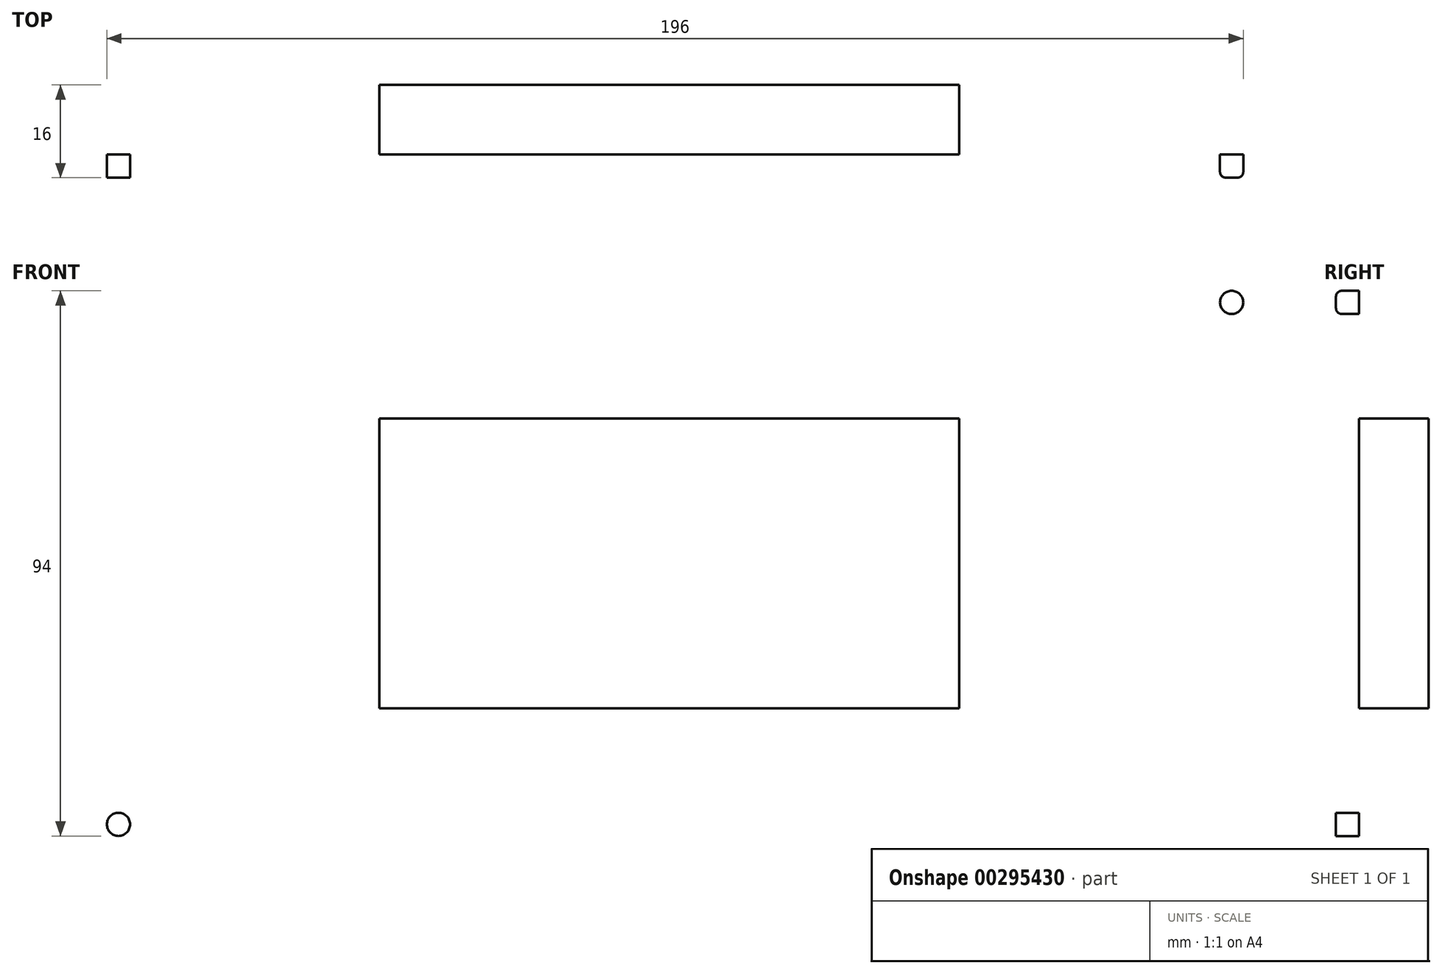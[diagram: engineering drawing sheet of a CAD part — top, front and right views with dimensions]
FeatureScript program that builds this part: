
annotation { "Feature Type Name" : "Feature", "Feature Type Description" : "" }
export const myFeature = defineFeature(function(context is Context, id is Id, definition is map)
    precondition{}
    {
        {
            var Q0;
            Q0=qCreatedBy(makeId("Front.planeOp"),FACE);
            var sketch = newSketch(context, id + "F0", { "sketchPlane" : qUnion([Q0])});
            skLineSegment(sketch, "E0.bottom", {"start": v(-188.88, 110.46) * mm, "end": v(13.12, 110.46) * mm});
            skLineSegment(sketch, "E0.top", {"start": v(-188.88, 10.46) * mm, "end": v(13.12, 10.46) * mm});
            skLineSegment(sketch, "E0.left", {"start": v(-188.88, 110.46) * mm, "end": v(-188.88, 10.46) * mm});
            skLineSegment(sketch, "E0.right", {"start": v(13.12, 110.46) * mm, "end": v(13.12, 10.46) * mm});
            skText(sketch, "E1", { "text": "// KARTA //", "fontName": "AllertaStencil-Regular.ttf"});
            const initialGuessF0  = {"E1": [-0.12488, 0.05579, 1, 0, 0.00936]};
            skSetInitialGuess(sketch, initialGuessF0);
            skSolve(sketch);
        }
        {
            var Q0;
            Q0=makeQuery(id+"F0.imprint","IMPRINT",FACE,{"disambiguationData":[TD([[makeQuery(id+"F0.imprint","IMPRINT",EDGE,{"derivedFrom":sQuery(id+"F0.wireOp",EDGE,"E0.bottom")}),-1.0]])]});
            extrude(context, id + "F1", {"entities" : qUnion([Q0]), "depth" : 4 * mm});
        }
        {
            var Q0;
            Q0=makeQuery(id+"F1.opExtrude","CAP_FACE",FACE,{"disambiguationData":[OSD([sQuery(id+"F0.wireOp",EDGE,"E0.bottom"),sQuery(id+"F0.wireOp",EDGE,"E0.top"),sQuery(id+"F0.wireOp",EDGE,"E0.left"),sQuery(id+"F0.wireOp",EDGE,"E0.right")])],"isStart":false});
            var sketch = newSketch(context, id + "F2", { "sketchPlane" : qUnion([Q0])});
            skLineSegment(sketch, "E2", {"start": v(-87.88, 10.46) * mm, "end": v(-87.88, 60.46) * mm, "construction": true});
            skPoint(sketch, "E2.endSnap0", {"position": v(-163.38, 60.46) * mm});
            skLineSegment(sketch, "E3", {"start": v(-163.38, 60.46) * mm, "end": v(-87.88, 60.46) * mm, "construction": true});
            skCircle(sketch, "E4", {"center": v(-183.88, 105.46) * mm, "radius": 2 * mm});
            skCircle(sketch, "E5.MirrorC", {"center": v(-183.88, 15.46) * mm, "radius": 2 * mm});
            skCircle(sketch, "E6.MirrorC", {"center": v(8.12, 105.46) * mm, "radius": 2 * mm});
            skCircle(sketch, "E7.MirrorC", {"center": v(8.12, 15.46) * mm, "radius": 2 * mm});
            skSolve(sketch);
        }
        {
            var Q0;
            Q0=makeQuery(id+"F2.imprint","IMPRINT",FACE,{"disambiguationData":[TD([[makeQuery(id+"F2.imprint","IMPRINT",EDGE,{"derivedFrom":sQuery(id+"F2.wireOp",EDGE,"E4")}),1.0]])]});
            var Q1;
            Q1=makeQuery(id+"F2.imprint","IMPRINT",FACE,{"disambiguationData":[TD([[makeQuery(id+"F2.imprint","IMPRINT",EDGE,{"derivedFrom":sQuery(id+"F2.wireOp",EDGE,"2b5eb0ab-fe42-49a6-bda5-95ec015d2c950.MirrorC")}),-1.0]])]});
            var Q2;
            Q2=makeQuery(id+"F2.imprint","IMPRINT",FACE,{"disambiguationData":[TD([[makeQuery(id+"F2.imprint","IMPRINT",EDGE,{"derivedFrom":sQuery(id+"F2.wireOp",EDGE,"2b5eb0ab-fe42-49a6-bda5-95ec015d2c951.MirrorC")}),1.0]])]});
            var Q3;
            Q3=makeQuery(id+"F2.imprint","IMPRINT",FACE,{"disambiguationData":[TD([[makeQuery(id+"F2.imprint","IMPRINT",EDGE,{"derivedFrom":sQuery(id+"F2.wireOp",EDGE,"E5.MirrorC")}),-1.0]])]});
            var Q4;
            Q4=makeQuery(id+"F2.imprint","IMPRINT",FACE,{"disambiguationData":[TD([[makeQuery(id+"F2.imprint","IMPRINT",EDGE,{"derivedFrom":sQuery(id+"F2.wireOp",EDGE,"V1kDyeQm-8hri-Xp3O-SjeW-TMvqUFOvwADP")}),1.0]])]});
            var Q5;
            Q5=makeQuery(id+"F2.imprint","IMPRINT",FACE,{"disambiguationData":[TD([[makeQuery(id+"F2.imprint","IMPRINT",EDGE,{"derivedFrom":sQuery(id+"F2.wireOp",EDGE,"Exs6iu4G-od2C-X4no-m5jr-fqEDQrViM3JW")}),1.0]])]});
            var Q6;
            Q6=makeQuery(id+"F2.imprint","IMPRINT",FACE,{"disambiguationData":[TD([[makeQuery(id+"F2.imprint","IMPRINT",EDGE,{"derivedFrom":sQuery(id+"F2.wireOp",EDGE,"ipAvfNOG-kqIk-37sJ-MxmZ-H9NNCKEkc3zR")}),1.0]])]});
            var Q7;
            Q7=makeQuery(id+"F2.imprint","IMPRINT",FACE,{"disambiguationData":[TD([[makeQuery(id+"F2.imprint","IMPRINT",EDGE,{"derivedFrom":sQuery(id+"F2.wireOp",EDGE,"hssNBFLj-hphz-50Qe-x43B-HVMR0uP99XgS")}),1.0]])]});
            var Q8;
            Q8=makeQuery(id+"F2.imprint","IMPRINT",FACE,{"disambiguationData":[TD([[makeQuery(id+"F2.imprint","IMPRINT",EDGE,{"derivedFrom":sQuery(id+"F2.wireOp",EDGE,"E6.MirrorC")}),-1.0]])]});
            var Q9;
            Q9=makeQuery(id+"F2.imprint","IMPRINT",FACE,{"disambiguationData":[TD([[makeQuery(id+"F2.imprint","IMPRINT",EDGE,{"derivedFrom":sQuery(id+"F2.wireOp",EDGE,"E7.MirrorC")}),1.0]])]});
            extrude(context, id + "F3", {"entities" : qUnion([Q0, Q1, Q2, Q3, Q4, Q5, Q6, Q7, Q8, Q9]), "operationType" : NewBodyOperationType.REMOVE, "oppositeDirection" : true, "depth" : 25 * mm});
        }
        {
            var Q0;
            Q0=makeQuery(id+"F3.boolean.opBoolean","COPY",EDGE,{"derivedFrom":makeQuery(id+"F3.opExtrude","CAP_EDGE",EDGE,{"disambiguationData":[OSD([sQuery(id+"F2.wireOp",EDGE,"E4")])],"isStart":true})});
            var Q1;
            Q1=makeQuery(id+"F3.boolean.opBoolean","COPY",EDGE,{"derivedFrom":makeQuery(id+"F3.opExtrude","CAP_EDGE",EDGE,{"disambiguationData":[OSD([sQuery(id+"F2.wireOp",EDGE,"E5.MirrorC")])],"isStart":true})});
            var Q2;
            Q2=makeQuery(id+"F3.boolean.opBoolean","COPY",EDGE,{"derivedFrom":makeQuery(id+"F3.opExtrude","CAP_EDGE",EDGE,{"disambiguationData":[OSD([sQuery(id+"F2.wireOp",EDGE,"E7.MirrorC")])],"isStart":true})});
            var Q3;
            Q3=makeQuery(id+"F3.boolean.opBoolean","COPY",EDGE,{"derivedFrom":makeQuery(id+"F3.opExtrude","CAP_EDGE",EDGE,{"disambiguationData":[OSD([sQuery(id+"F2.wireOp",EDGE,"E6.MirrorC")])],"isStart":true})});
            fillet(context, id + "F4", {"entities" : qUnion([Q0, Q1, Q2, Q3]), "radius" : 1 * mm, "tangentPropagation" : true, "allowEdgeOverflow" : false});
        }
        {
            var Q0;
            Q0=qCreatedBy(makeId("Front.planeOp"),FACE);
            cPlane(context, id + "F5", {"entities" : qUnion([Q0]), "cplaneType" : CPlaneType.OFFSET, "offset" : 0 * mm, "oppositeDirection" : true, "width" : 150 * mm, "height" : 150 * mm});
        }
        {
            var Q0;
            Q0=qCreatedBy(id+"F5.planeOp",FACE);
            var sketch = newSketch(context, id + "F6", { "sketchPlane" : qUnion([Q0])});
            skLineSegment(sketch, "E8.bottom", {"start": v(-38.88, 85.46) * mm, "end": v(-138.88, 85.46) * mm});
            skLineSegment(sketch, "E8.top", {"start": v(-38.88, 35.46) * mm, "end": v(-138.88, 35.46) * mm});
            skLineSegment(sketch, "E8.left", {"start": v(-38.88, 85.46) * mm, "end": v(-38.88, 35.46) * mm});
            skLineSegment(sketch, "E8.right", {"start": v(-138.88, 85.46) * mm, "end": v(-138.88, 35.46) * mm});
            skSolve(sketch);
        }
        {
            var Q0;
            Q0 = qSketchRegion(id + "F6", true);
            extrude(context, id + "F7", {"entities" : qUnion([Q0]), "oppositeDirection" : true, "depth" : 12 * mm});
        }
    });
